# Revit family: Water Outlet_Face Based_Agrob Buchtal_Wiesbaden System_Silent W 2000
name_source: partatom
category: Generic Models
revit_build: Autodesk Revit 2014 (Build: 20130308_1515(x64)
units: mm (PartAtom-declared; Revit-internal decimal feet)

## types (1)
- Water Outlet_Face Based_Agrob Buchtal_Wiesbaden System_Silent W 2000
    BIMobject category = Swimming pool
    Default Elevation = 1219 mm
    Design country = Germany
    Edition number = 1
    Manufacturer country = Germany
    Manufacturer name = AGROB BUCHTAL
    Material main = Ceramics
    NBS Reference Code = 50-24-24
    NBS Reference Description = Drainage Channels With Gratings
    Nominal height = 0
    Nominal width = 0
    OmniClass Code = 23-39 29 15
    OmniClass Description = Waste Water Channels, Gullies, Gratings, Covers
    Outlet Valve Material = White
    Product Guid = d2edff46-8a1b-4956-9a74-b639ebe51e18
    Product SKU = Wiesbaden
    Product data url = https://bimobject.com
    Product family = Swimming pool ceramics
    Product group = Pool edge systems
    QR code = http://bimobject.com
    Technical description = http://www.agrob-buchtal.de
    UNSPSC Code = 3018
    Uniclass 1.4 Code = JR1
    Uniclass 1.4 Description = Drainage
    Uniclass 2.0 Code = PR-50-24-24
    Uniclass 2.0 Description = Drainage Channels With Gratings
    Weight Net (Kg) = 0

## geometry (parser evidence)
native form markers: Sweep x4
no freeform markers — native parametric forms only
